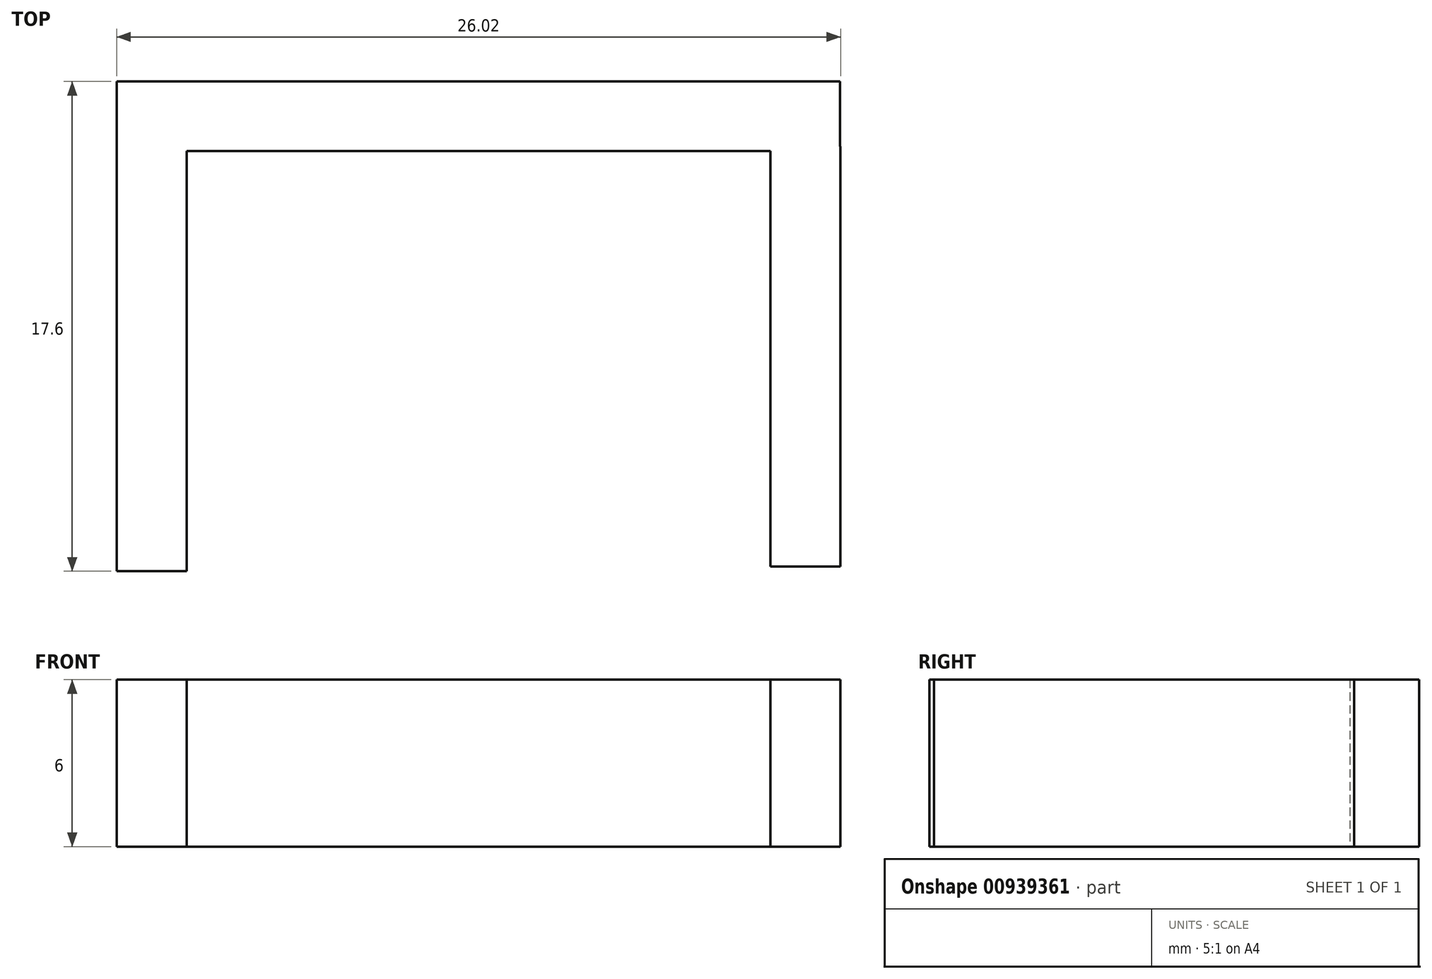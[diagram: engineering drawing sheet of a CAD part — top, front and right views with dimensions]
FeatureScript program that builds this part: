
annotation { "Feature Type Name" : "Feature", "Feature Type Description" : "" }
export const myFeature = defineFeature(function(context is Context, id is Id, definition is map)
    precondition{}
    {
        {
            var Q0;
            Q0=qCreatedBy(makeId("Top.planeOp"),FACE);
            var sketch = newSketch(context, id + "F0", { "sketchPlane" : qUnion([Q0])});
            skLineSegment(sketch, "E0.bottom", {"start": v(13, 1.94) * mm, "end": v(-13, 1.94) * mm});
            skLineSegment(sketch, "E0.top", {"start": v(13, -0.56) * mm, "end": v(-13, -0.56) * mm});
            skLineSegment(sketch, "E0.left", {"start": v(13, 1.94) * mm, "end": v(13, -0.56) * mm});
            skLineSegment(sketch, "E0.right", {"start": v(-13, 1.94) * mm, "end": v(-13, -0.56) * mm});
            skPoint(sketch, "E0.middle", {"position": v(0, 0.7) * mm});
            skLineSegment(sketch, "E1", {"start": v(-13, -0.56) * mm, "end": v(-10.48, -0.56) * mm});
            skLineSegment(sketch, "E2", {"start": v(-10.48, -0.56) * mm, "end": v(-10.48, -15.66) * mm});
            skLineSegment(sketch, "E3", {"start": v(-10.48, -15.66) * mm, "end": v(-13, -15.66) * mm});
            skLineSegment(sketch, "E4", {"start": v(-13, -15.66) * mm, "end": v(-13, -0.56) * mm});
            skLineSegment(sketch, "E5.1.0.0", {"start": v(10.5, -15.5) * mm, "end": v(10.5, -0.4) * mm});
            skLineSegment(sketch, "E5.1.0.1", {"start": v(13.02, -0.4) * mm, "end": v(13.02, -15.5) * mm});
            skLineSegment(sketch, "E5.direction1", {"start": v(-13, -15.66) * mm, "end": v(10.5, -15.5) * mm, "construction": true});
            skLineSegment(sketch, "E6", {"start": v(10.5, -0.4) * mm, "end": v(13.02, -0.4) * mm});
            skLineSegment(sketch, "E7", {"start": v(10.5, -15.5) * mm, "end": v(13.02, -15.5) * mm});
            skSolve(sketch);
        }
        {
            var Q0;
            {var subQ1=sQuery(id+"F0.wireOp",EDGE,"E0.bottom");Q0=makeQuery(id+"F0.imprint","IMPRINT",FACE,{"disambiguationData":[TD([[makeQuery(id+"F0.imprint","IMPRINT",EDGE,{"derivedFrom":subQ1}),1.0]])]});}
            var Q1;
            {var subQ2=sQuery(id+"F0.wireOp",EDGE,"E2");Q1=makeQuery(id+"F0.imprint","IMPRINT",FACE,{"disambiguationData":[TD([[makeQuery(id+"F0.imprint","IMPRINT",EDGE,{"derivedFrom":subQ2}),-1.0]])]});}
            var Q2;
            {var subQ0=sQuery(id+"F0.wireOp",EDGE,"E5.1.0.1");Q2=makeQuery(id+"F0.imprint","IMPRINT",FACE,{"disambiguationData":[TD([[makeQuery(id+"F0.imprint","IMPRINT",EDGE,{"derivedFrom":subQ0}),-1.0]])]});}
            var Q3;
            {var subQ0=sQuery(id+"F0.wireOp",EDGE,"E5.1.0.0");var subQ1=sQuery(id+"F0.wireOp",EDGE,"E0.top");var subQ2=makeQuery(id+"F0.imprint","INTERSECT",VERTEX,{"derivedFrom":[subQ1,subQ0]});Q3=makeQuery(id+"F0.imprint","IMPRINT",FACE,{"disambiguationData":[TD([[makeQuery(id+"F0.imprint","IMPRINT",EDGE,{"disambiguationData":[TD([[subQ2,1.0]])],"derivedFrom":subQ1}),-1.0]])]});}
            extrude(context, id + "F1", {"entities" : qUnion([Q0, Q1, Q2, Q3]), "depth" : 6 * mm, "offsetDistance" : 25 * mm});
        }
    });
